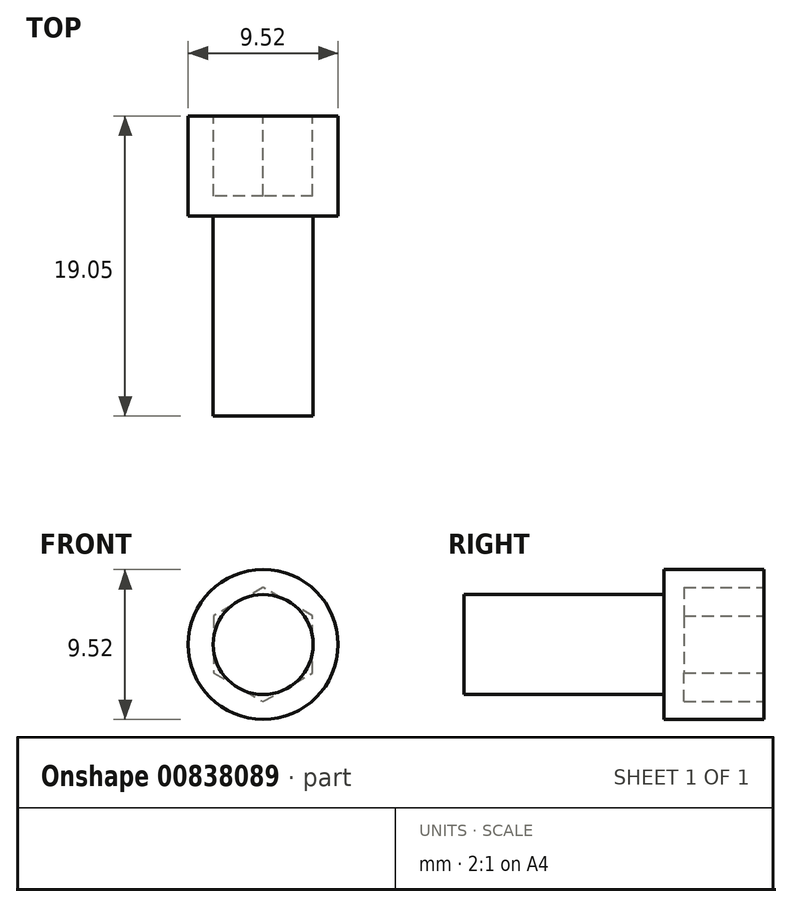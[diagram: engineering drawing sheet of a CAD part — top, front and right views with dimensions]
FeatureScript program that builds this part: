
annotation { "Feature Type Name" : "Feature", "Feature Type Description" : "" }
export const myFeature = defineFeature(function(context is Context, id is Id, definition is map)
    precondition{}
    {
        {
            var Q0;
            Q0=qCreatedBy(makeId("Front.planeOp"),FACE);
            var sketch = newSketch(context, id + "F0", { "sketchPlane" : qUnion([Q0])});
            skCircle(sketch, "E0", {"center": v(0, 0) * mm, "radius": 4.76 * mm});
            skSolve(sketch);
        }
        {
            var Q0;
            Q0=makeQuery(id+"F0.imprint","IMPRINT",FACE,{"disambiguationData":[TD([[makeQuery(id+"F0.imprint","IMPRINT",EDGE,{"derivedFrom":sQuery(id+"F0.wireOp",EDGE,"E0")}),1.0]])]});
            extrude(context, id + "F1", {"entities" : qUnion([Q0]), "depth" : 6.35 * mm, "offsetDistance" : 25.4 * mm});
        }
        {
            var Q0;
            Q0=makeQuery(id+"F1.opExtrude","CAP_FACE",FACE,{"disambiguationData":[OSD([sQuery(id+"F0.wireOp",EDGE,"E0")])],"isStart":false});
            var sketch = newSketch(context, id + "F2", { "sketchPlane" : qUnion([Q0])});
            skCircle(sketch, "E1", {"center": v(0, 0) * mm, "radius": 3.18 * mm});
            skSolve(sketch);
        }
        {
            var Q0;
            Q0=makeQuery(id+"F2.imprint","IMPRINT",FACE,{"disambiguationData":[TD([[makeQuery(id+"F2.imprint","IMPRINT",EDGE,{"derivedFrom":sQuery(id+"F2.wireOp",EDGE,"E1")}),1.0]])]});
            extrude(context, id + "F3", {"entities" : qUnion([Q0]), "operationType" : NewBodyOperationType.ADD, "depth" : 12.7 * mm, "offsetDistance" : 25.4 * mm});
        }
        {
            var Q0;
            Q0=makeQuery(id+"F1.opExtrude","CAP_FACE",FACE,{"disambiguationData":[OSD([sQuery(id+"F0.wireOp",EDGE,"E0")])],"isStart":true});
            var sketch = newSketch(context, id + "F4", { "sketchPlane" : qUnion([Q0])});
            skCircle(sketch, "E2.cCircle", {"center": v(0, 0) * mm, "radius": 3.14 * mm, "construction": true});
            skLineSegment(sketch, "E2.0", {"start": v(3.14, 1.81) * mm, "end": v(3.14, -1.81) * mm});
            skLineSegment(sketch, "E2.1", {"start": v(3.14, -1.81) * mm, "end": v(0, -3.63) * mm});
            skLineSegment(sketch, "E2.2", {"start": v(0, -3.63) * mm, "end": v(-3.14, -1.81) * mm});
            skLineSegment(sketch, "E2.3", {"start": v(-3.14, -1.81) * mm, "end": v(-3.14, 1.81) * mm});
            skLineSegment(sketch, "E2.4", {"start": v(-3.14, 1.81) * mm, "end": v(0, 3.63) * mm});
            skLineSegment(sketch, "E2.5", {"start": v(0, 3.63) * mm, "end": v(3.14, 1.81) * mm});
            skPoint(sketch, "E2.0.midPoint", {"position": v(3.14, 0) * mm});
            skSolve(sketch);
        }
        {
            var Q0;
            Q0=makeQuery(id+"F4.imprint","IMPRINT",FACE,{"disambiguationData":[TD([[makeQuery(id+"F4.imprint","IMPRINT",EDGE,{"derivedFrom":sQuery(id+"F4.wireOp",EDGE,"E2.0")}),-1.0]])]});
            extrude(context, id + "F5", {"entities" : qUnion([Q0]), "operationType" : NewBodyOperationType.REMOVE, "oppositeDirection" : true, "depth" : 5.08 * mm, "offsetDistance" : 25.4 * mm});
        }
    });
